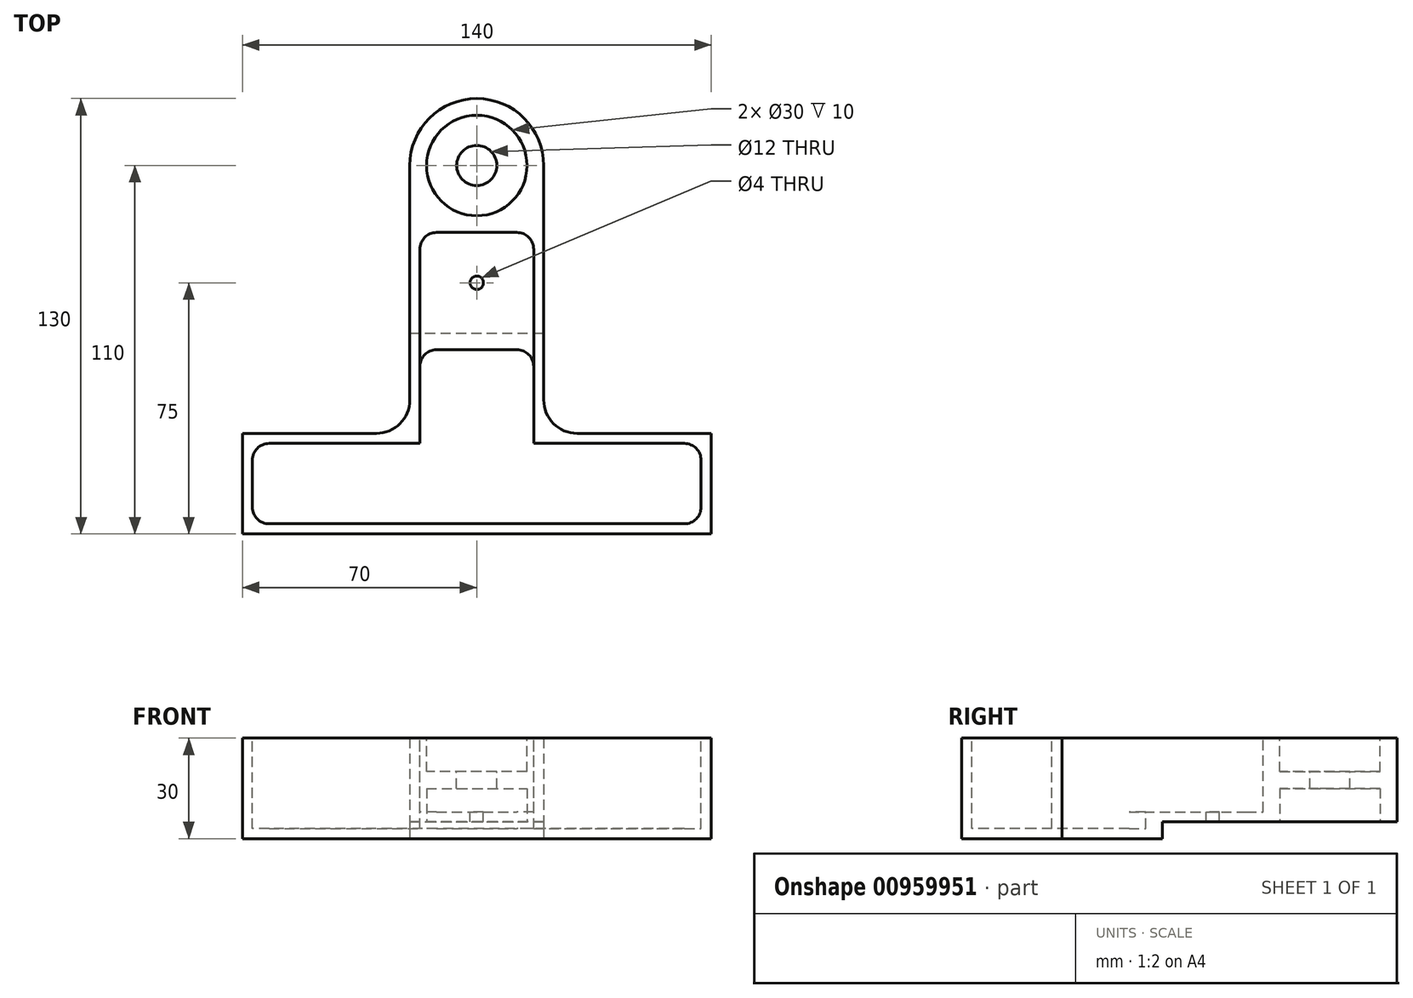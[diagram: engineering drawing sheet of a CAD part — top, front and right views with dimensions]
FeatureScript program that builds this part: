
annotation { "Feature Type Name" : "Feature", "Feature Type Description" : "" }
export const myFeature = defineFeature(function(context is Context, id is Id, definition is map)
    precondition{}
    {
        {
            var Q0;
            Q0=qCreatedBy(makeId("Top.planeOp"),FACE);
            var sketch = newSketch(context, id + "F0", { "sketchPlane" : qUnion([Q0])});
            skArc(sketch, "E0", {"start": v(20, 110) * mm, "mid": v(0, 130) * mm, "end": v(-20, 110) * mm});
            skLineSegment(sketch, "E1", {"start": v(20, 110) * mm, "end": v(20, 30) * mm});
            skLineSegment(sketch, "E2", {"start": v(20, 30) * mm, "end": v(70, 30) * mm});
            skLineSegment(sketch, "E3", {"start": v(70, 30) * mm, "end": v(70, 0) * mm});
            skLineSegment(sketch, "E4", {"start": v(70, 0) * mm, "end": v(-70, 0) * mm});
            skLineSegment(sketch, "E5", {"start": v(-70, 0) * mm, "end": v(-70, 30) * mm});
            skLineSegment(sketch, "E6", {"start": v(-70, 30) * mm, "end": v(-20, 30) * mm});
            skLineSegment(sketch, "E7", {"start": v(-20, 30) * mm, "end": v(-20, 110) * mm});
            skLineSegment(sketch, "E8", {"start": v(0, 0) * mm, "end": v(0, -46.03) * mm, "construction": true});
            skCircle(sketch, "E9", {"center": v(0, 75) * mm, "radius": 15 * mm, "construction": true});
            skCircle(sketch, "E10", {"center": v(0, 110) * mm, "radius": 15 * mm, "construction": true});
            skLineSegment(sketch, "E11.bottom", {"start": v(-67, 22) * mm, "end": v(-23, 22) * mm, "construction": true});
            skLineSegment(sketch, "E11.top", {"start": v(-67, 8) * mm, "end": v(-23, 8) * mm, "construction": true});
            skLineSegment(sketch, "E11.left", {"start": v(-67, 22) * mm, "end": v(-67, 8) * mm, "construction": true});
            skLineSegment(sketch, "E11.right", {"start": v(-23, 22) * mm, "end": v(-23, 8) * mm, "construction": true});
            skLineSegment(sketch, "E12", {"start": v(-67, 15) * mm, "end": v(-70, 15) * mm, "construction": true});
            skLineSegment(sketch, "E13.MirrorCS", {"start": v(23, 22) * mm, "end": v(23, 8) * mm, "construction": true});
            skLineSegment(sketch, "E14.MirrorCS", {"start": v(67, 8) * mm, "end": v(23, 8) * mm, "construction": true});
            skLineSegment(sketch, "E15.MirrorCS", {"start": v(67, 22) * mm, "end": v(23, 22) * mm, "construction": true});
            skLineSegment(sketch, "E16.MirrorCS", {"start": v(67, 22) * mm, "end": v(67, 8) * mm, "construction": true});
            skSolve(sketch);
        }
        {
            var Q0;
            Q0 = qSketchRegion(id + "F0", true);
            extrude(context, id + "F1", {"entities" : qUnion([Q0]), "depth" : 30 * mm, "offsetDistance" : 25 * mm});
        }
        {
            var Q0;
            Q0=makeQuery(id+"F0.imprint","IMPRINT",FACE,{"disambiguationData":[TD([[makeQuery(id+"F0.imprint","IMPRINT",EDGE,{"derivedFrom":sQuery(id+"F0.wireOp",EDGE,"E0")}),1.0]])]});
            var sketch = newSketch(context, id + "F2", { "sketchPlane" : qUnion([Q0])});
            skLineSegment(sketch, "E17.bottom", {"start": v(-20, 130) * mm, "end": v(20, 130) * mm});
            skLineSegment(sketch, "E17.top", {"start": v(-20, 60) * mm, "end": v(20, 60) * mm});
            skLineSegment(sketch, "E17.left", {"start": v(-20, 130) * mm, "end": v(-20, 60) * mm});
            skLineSegment(sketch, "E17.right", {"start": v(20, 130) * mm, "end": v(20, 60) * mm});
            skSolve(sketch);
        }
        {
            var Q0;
            Q0 = qSketchRegion(id + "F2", true);
            extrude(context, id + "F3", {"entities" : qUnion([Q0]), "operationType" : NewBodyOperationType.REMOVE, "depth" : 5 * mm, "offsetDistance" : 25 * mm});
        }
        {
            var Q0;
            Q0=makeQuery(id+"F1.opExtrude","CAP_FACE",FACE,{"disambiguationData":[OSD([sQuery(id+"F0.wireOp",EDGE,"E0"),sQuery(id+"F0.wireOp",EDGE,"E1"),sQuery(id+"F0.wireOp",EDGE,"E2"),sQuery(id+"F0.wireOp",EDGE,"E3"),sQuery(id+"F0.wireOp",EDGE,"E4"),sQuery(id+"F0.wireOp",EDGE,"E5"),sQuery(id+"F0.wireOp",EDGE,"E6"),sQuery(id+"F0.wireOp",EDGE,"E7")])],"isStart":false});
            var sketch = newSketch(context, id + "F4", { "sketchPlane" : qUnion([Q0])});
            skLineSegment(sketch, "E18.0", {"start": v(-17, 27) * mm, "end": v(-17, 55) * mm});
            skLineSegment(sketch, "E18.1", {"start": v(-67, 27) * mm, "end": v(-17, 27) * mm});
            skLineSegment(sketch, "E18.2", {"start": v(-67, 3) * mm, "end": v(-67, 27) * mm});
            skLineSegment(sketch, "E18.3", {"start": v(17, 55) * mm, "end": v(17, 27) * mm});
            skLineSegment(sketch, "E18.4", {"start": v(17, 27) * mm, "end": v(67, 27) * mm});
            skLineSegment(sketch, "E18.5", {"start": v(67, 27) * mm, "end": v(67, 3) * mm});
            skLineSegment(sketch, "E18.6", {"start": v(67, 3) * mm, "end": v(-67, 3) * mm});
            skLineSegment(sketch, "E19", {"start": v(-17, 55) * mm, "end": v(17, 55) * mm});
            skSolve(sketch);
        }
        {
            var Q0;
            Q0 = qSketchRegion(id + "F4", true);
            extrude(context, id + "F5", {"entities" : qUnion([Q0]), "operationType" : NewBodyOperationType.REMOVE, "oppositeDirection" : true, "depth" : 27 * mm, "offsetDistance" : 25 * mm});
        }
        {
            var Q0;
            Q0=makeQuery(id+"F1.opExtrude","CAP_FACE",FACE,{"disambiguationData":[OSD([sQuery(id+"F0.wireOp",EDGE,"E0"),sQuery(id+"F0.wireOp",EDGE,"E1"),sQuery(id+"F0.wireOp",EDGE,"E2"),sQuery(id+"F0.wireOp",EDGE,"E3"),sQuery(id+"F0.wireOp",EDGE,"E4"),sQuery(id+"F0.wireOp",EDGE,"E5"),sQuery(id+"F0.wireOp",EDGE,"E6"),sQuery(id+"F0.wireOp",EDGE,"E7")])],"isStart":false});
            var sketch = newSketch(context, id + "F6", { "sketchPlane" : qUnion([Q0])});
            skLineSegment(sketch, "E20.bottom", {"start": v(-17, 55) * mm, "end": v(17, 55) * mm});
            skLineSegment(sketch, "E20.top", {"start": v(-17, 90) * mm, "end": v(17, 90) * mm});
            skLineSegment(sketch, "E20.left", {"start": v(-17, 55) * mm, "end": v(-17, 90) * mm});
            skLineSegment(sketch, "E20.right", {"start": v(17, 55) * mm, "end": v(17, 90) * mm});
            skSolve(sketch);
        }
        {
            var Q0;
            Q0 = qSketchRegion(id + "F6", true);
            extrude(context, id + "F7", {"entities" : qUnion([Q0]), "operationType" : NewBodyOperationType.REMOVE, "oppositeDirection" : true, "depth" : 22 * mm, "offsetDistance" : 25 * mm});
        }
        {
            var Q0;
            Q0=makeQuery(id+"F1.opExtrude","CAP_FACE",FACE,{"disambiguationData":[OSD([sQuery(id+"F0.wireOp",EDGE,"E0"),sQuery(id+"F0.wireOp",EDGE,"E1"),sQuery(id+"F0.wireOp",EDGE,"E2"),sQuery(id+"F0.wireOp",EDGE,"E3"),sQuery(id+"F0.wireOp",EDGE,"E4"),sQuery(id+"F0.wireOp",EDGE,"E5"),sQuery(id+"F0.wireOp",EDGE,"E6"),sQuery(id+"F0.wireOp",EDGE,"E7")])],"isStart":false});
            var sketch = newSketch(context, id + "F8", { "sketchPlane" : qUnion([Q0])});
            skCircle(sketch, "E21.0", {"center": v(0, 110) * mm, "radius": 15 * mm});
            skSolve(sketch);
        }
        {
            var Q0;
            Q0 = qSketchRegion(id + "F8", true);
            extrude(context, id + "F9", {"entities" : qUnion([Q0]), "operationType" : NewBodyOperationType.REMOVE, "oppositeDirection" : true, "depth" : 10 * mm, "offsetDistance" : 25 * mm});
        }
        {
            var Q0;
            Q0=makeQuery(id+"F1.opExtrude","CAP_FACE",FACE,{"disambiguationData":[OSD([sQuery(id+"F0.wireOp",EDGE,"E0"),sQuery(id+"F0.wireOp",EDGE,"E1"),sQuery(id+"F0.wireOp",EDGE,"E2"),sQuery(id+"F0.wireOp",EDGE,"E3"),sQuery(id+"F0.wireOp",EDGE,"E4"),sQuery(id+"F0.wireOp",EDGE,"E5"),sQuery(id+"F0.wireOp",EDGE,"E6"),sQuery(id+"F0.wireOp",EDGE,"E7")])],"isStart":false});
            var sketch = newSketch(context, id + "F10", { "sketchPlane" : qUnion([Q0])});
            skCircle(sketch, "E22", {"center": v(0, 110) * mm, "radius": 6 * mm});
            skSolve(sketch);
        }
        {
            var Q0;
            Q0 = qSketchRegion(id + "F10", true);
            extrude(context, id + "F11", {"entities" : qUnion([Q0]), "operationType" : NewBodyOperationType.REMOVE, "endBound" : BoundingType.THROUGH_ALL, "oppositeDirection" : true, "depth" : 25 * mm, "offsetDistance" : 25 * mm});
        }
        {
            var Q0;
            Q0=makeQuery(id+"F1.opExtrude","SWEPT_EDGE",EDGE,{"disambiguationData":[OSD([sQuery(id+"F0.wireOp",EDGE,"E1"),sQuery(id+"F0.wireOp",EDGE,"E2")])]});
            var Q1;
            Q1=makeQuery(id+"F1.opExtrude","SWEPT_EDGE",EDGE,{"disambiguationData":[OSD([sQuery(id+"F0.wireOp",EDGE,"E6"),sQuery(id+"F0.wireOp",EDGE,"E7")])]});
            fillet(context, id + "F12", {"entities" : qUnion([Q0, Q1]), "radius" : 10 * mm, "tangentPropagation" : true, "allowEdgeOverflow" : false});
        }
        {
            var Q0;
            Q0=makeQuery(id+"F7.boolean.opBoolean","COPY",EDGE,{"derivedFrom":makeQuery(id+"F7.opExtrude","SWEPT_EDGE",EDGE,{"disambiguationData":[OSD([sQuery(id+"F6.wireOp",EDGE,"E20.top"),sQuery(id+"F6.wireOp",EDGE,"E20.left")])]})});
            var Q1;
            Q1=makeQuery(id+"F5.boolean.opBoolean","COPY",EDGE,{"derivedFrom":makeQuery(id+"F5.opExtrude","SWEPT_EDGE",EDGE,{"disambiguationData":[OSD([sQuery(id+"F4.wireOp",EDGE,"E18.1"),sQuery(id+"F4.wireOp",EDGE,"E18.2")])]})});
            var Q2;
            Q2=makeQuery(id+"F7.boolean.opBoolean","COPY",EDGE,{"derivedFrom":makeQuery(id+"F7.opExtrude","SWEPT_EDGE",EDGE,{"disambiguationData":[OSD([sQuery(id+"F6.wireOp",EDGE,"E20.top"),sQuery(id+"F6.wireOp",EDGE,"E20.right")])]})});
            var Q3;
            Q3=makeQuery(id+"F5.boolean.opBoolean","COPY",EDGE,{"derivedFrom":makeQuery(id+"F5.opExtrude","SWEPT_EDGE",EDGE,{"disambiguationData":[OSD([sQuery(id+"F4.wireOp",EDGE,"E18.4"),sQuery(id+"F4.wireOp",EDGE,"E18.5")])]})});
            var Q4;
            Q4=makeQuery(id+"F5.boolean.opBoolean","COPY",EDGE,{"derivedFrom":makeQuery(id+"F5.opExtrude","SWEPT_EDGE",EDGE,{"disambiguationData":[OSD([sQuery(id+"F4.wireOp",EDGE,"E18.2"),sQuery(id+"F4.wireOp",EDGE,"E18.6")])]})});
            var Q5;
            Q5=makeQuery(id+"F5.boolean.opBoolean","COPY",EDGE,{"derivedFrom":makeQuery(id+"F5.opExtrude","SWEPT_EDGE",EDGE,{"disambiguationData":[OSD([sQuery(id+"F4.wireOp",EDGE,"E18.5"),sQuery(id+"F4.wireOp",EDGE,"E18.6")])]})});
            var Q6;
            Q6=makeQuery(id+"F5.boolean.opBoolean","COPY",EDGE,{"derivedFrom":makeQuery(id+"F5.opExtrude","SWEPT_EDGE",EDGE,{"disambiguationData":[OSD([sQuery(id+"F4.wireOp",EDGE,"E18.0"),sQuery(id+"F4.wireOp",EDGE,"E19")])]})});
            var Q7;
            Q7=makeQuery(id+"F5.boolean.opBoolean","COPY",EDGE,{"derivedFrom":makeQuery(id+"F5.opExtrude","SWEPT_EDGE",EDGE,{"disambiguationData":[OSD([sQuery(id+"F4.wireOp",EDGE,"E18.3"),sQuery(id+"F4.wireOp",EDGE,"E19")])]})});
            fillet(context, id + "F13", {"entities" : qUnion([Q0, Q1, Q2, Q3, Q4, Q5, Q6, Q7]), "radius" : 5 * mm, "tangentPropagation" : true, "allowEdgeOverflow" : false});
        }
        {
            var Q0;
            Q0=makeQuery(id+"F3.boolean.opBoolean","COPY",FACE,{"derivedFrom":makeQuery(id+"F3.opExtrude","CAP_FACE",FACE,{"disambiguationData":[OSD([sQuery(id+"F2.wireOp",EDGE,"E17.bottom"),sQuery(id+"F2.wireOp",EDGE,"E17.top"),sQuery(id+"F2.wireOp",EDGE,"E17.left"),sQuery(id+"F2.wireOp",EDGE,"E17.right")])],"isStart":false})});
            var sketch = newSketch(context, id + "F14", { "sketchPlane" : qUnion([Q0])});
            skCircle(sketch, "E23.0", {"center": v(0, -110) * mm, "radius": 15 * mm});
            skSolve(sketch);
        }
        {
            var Q0;
            Q0 = qSketchRegion(id + "F14", true);
            extrude(context, id + "F15", {"entities" : qUnion([Q0]), "operationType" : NewBodyOperationType.REMOVE, "oppositeDirection" : true, "depth" : 10 * mm, "offsetDistance" : 25 * mm});
        }
        {
            var Q0;
            Q0=makeQuery(id+"F7.boolean.opBoolean","COPY",FACE,{"derivedFrom":makeQuery(id+"F7.opExtrude","CAP_FACE",FACE,{"disambiguationData":[OSD([sQuery(id+"F6.wireOp",EDGE,"E20.bottom"),sQuery(id+"F6.wireOp",EDGE,"E20.top"),sQuery(id+"F6.wireOp",EDGE,"E20.left"),sQuery(id+"F6.wireOp",EDGE,"E20.right")])],"isStart":false})});
            var sketch = newSketch(context, id + "F16", { "sketchPlane" : qUnion([Q0])});
            skCircle(sketch, "E24", {"center": v(0, 75) * mm, "radius": 2 * mm});
            skSolve(sketch);
        }
        {
            var Q0;
            Q0 = qSketchRegion(id + "F16", true);
            extrude(context, id + "F17", {"entities" : qUnion([Q0]), "operationType" : NewBodyOperationType.REMOVE, "endBound" : BoundingType.THROUGH_ALL, "oppositeDirection" : true, "depth" : 25 * mm, "offsetDistance" : 25 * mm});
        }
    });
